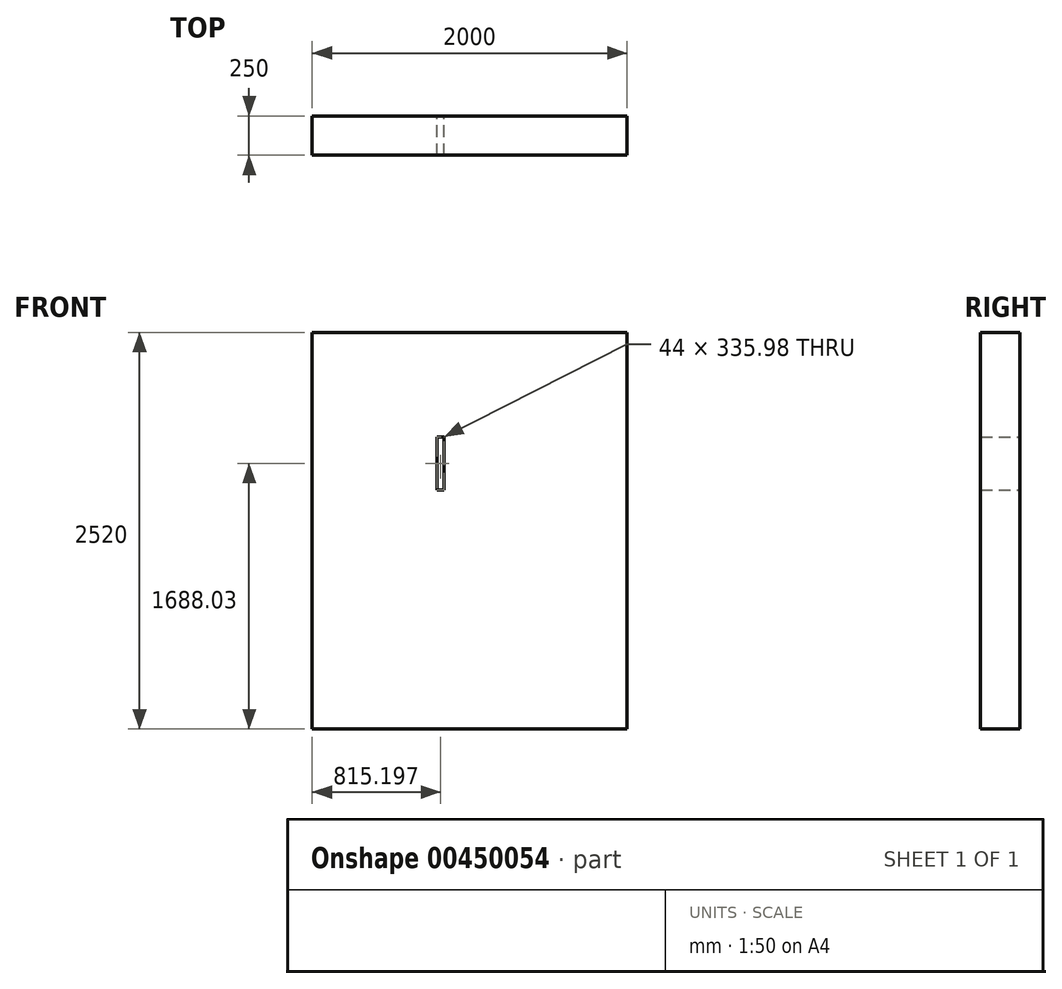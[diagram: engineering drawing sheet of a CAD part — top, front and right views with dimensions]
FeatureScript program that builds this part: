
annotation { "Feature Type Name" : "Feature", "Feature Type Description" : "" }
export const myFeature = defineFeature(function(context is Context, id is Id, definition is map)
    precondition{}
    {
        {
            var Q0;
            Q0=qCreatedBy(makeId("Front.planeOp"),FACE);
            var sketch = newSketch(context, id + "F0", { "sketchPlane" : qUnion([Q0])});
            skLineSegment(sketch, "E0.bottom", {"start": v(-1005.34, 1231.1) * mm, "end": v(994.66, 1231.1) * mm});
            skLineSegment(sketch, "E0.top", {"start": v(-1005.34, -1288.9) * mm, "end": v(994.66, -1288.9) * mm});
            skLineSegment(sketch, "E0.left", {"start": v(-1005.34, 1231.1) * mm, "end": v(-1005.34, -1288.9) * mm});
            skLineSegment(sketch, "E0.right", {"start": v(994.66, 1231.1) * mm, "end": v(994.66, -1288.9) * mm});
            skLineSegment(sketch, "E1.bottom", {"start": v(-168.14, 567.12) * mm, "end": v(-168.14, 231.14) * mm});
            skLineSegment(sketch, "E1.top", {"start": v(-212.14, 567.12) * mm, "end": v(-212.14, 231.14) * mm});
            skLineSegment(sketch, "E1.left", {"start": v(-168.14, 567.12) * mm, "end": v(-212.14, 567.12) * mm});
            skLineSegment(sketch, "E1.right", {"start": v(-168.14, 231.14) * mm, "end": v(-212.14, 231.14) * mm});
            skSolve(sketch);
        }
        {
            var Q0;
            Q0=makeQuery(id+"F0.imprint","IMPRINT",FACE,{"disambiguationData":[TD([[makeQuery(id+"F0.imprint","IMPRINT",EDGE,{"derivedFrom":sQuery(id+"F0.wireOp",EDGE,"E0.bottom")}),-1.0]])]});
            extrude(context, id + "F1", {"entities" : qUnion([Q0]), "depth" : 250 * mm});
        }
    });
